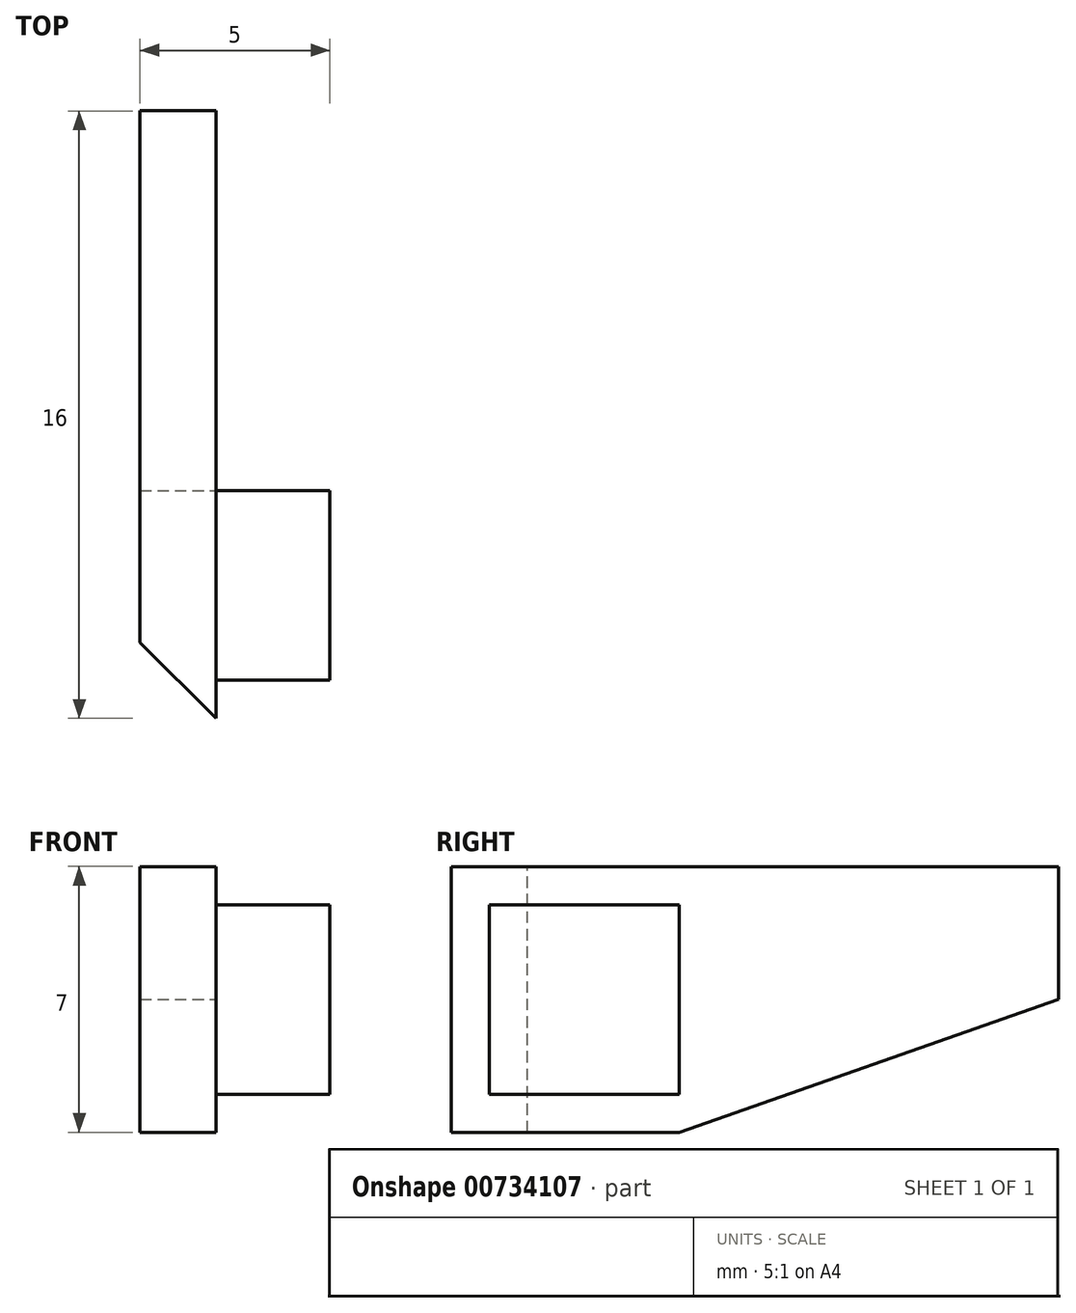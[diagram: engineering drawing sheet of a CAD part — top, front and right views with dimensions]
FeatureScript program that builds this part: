
annotation { "Feature Type Name" : "Feature", "Feature Type Description" : "" }
export const myFeature = defineFeature(function(context is Context, id is Id, definition is map)
    precondition{}
    {
        {
            var Q0;
            Q0=qCreatedBy(makeId("Right.planeOp"),FACE);
            var sketch = newSketch(context, id + "F0", { "sketchPlane" : qUnion([Q0])});
            skLineSegment(sketch, "E0.bottom", {"start": v(43.1, 34.6) * mm, "end": v(38.1, 34.6) * mm});
            skLineSegment(sketch, "E0.top", {"start": v(43.1, 29.6) * mm, "end": v(38.1, 29.6) * mm});
            skLineSegment(sketch, "E0.left", {"start": v(43.1, 34.6) * mm, "end": v(43.1, 29.6) * mm});
            skLineSegment(sketch, "E0.right", {"start": v(38.1, 34.6) * mm, "end": v(38.1, 29.6) * mm});
            skSolve(sketch);
        }
        {
            var Q0;
            Q0=makeQuery(id+"F0.imprint","IMPRINT",FACE,{"disambiguationData":[TD([[makeQuery(id+"F0.imprint","IMPRINT",EDGE,{"derivedFrom":sQuery(id+"F0.wireOp",EDGE,"E0.bottom")}),1.0]])]});
            extrude(context, id + "F1", {"entities" : qUnion([Q0]), "depth" : 3 * mm, "offsetDistance" : 25 * mm});
        }
        {
            var Q0;
            Q0=makeQuery(id+"F1.opExtrude","CAP_FACE",FACE,{"disambiguationData":[OSD([sQuery(id+"F0.wireOp",EDGE,"E0.bottom"),sQuery(id+"F0.wireOp",EDGE,"E0.top"),sQuery(id+"F0.wireOp",EDGE,"E0.left"),sQuery(id+"F0.wireOp",EDGE,"E0.right")])],"isStart":true});
            var sketch = newSketch(context, id + "F2", { "sketchPlane" : qUnion([Q0])});
            skLineSegment(sketch, "E1.bottom", {"start": v(-37.1, 35.6) * mm, "end": v(-53.1, 35.6) * mm});
            skLineSegment(sketch, "E1.top", {"start": v(-37.1, 28.6) * mm, "end": v(-53.1, 28.6) * mm});
            skLineSegment(sketch, "E1.left", {"start": v(-37.1, 35.6) * mm, "end": v(-37.1, 28.6) * mm});
            skLineSegment(sketch, "E1.right", {"start": v(-53.1, 35.6) * mm, "end": v(-53.1, 28.6) * mm});
            skLineSegment(sketch, "E2", {"start": v(-53.1, 32.1) * mm, "end": v(-43.1, 35.6) * mm});
            skLineSegment(sketch, "E3", {"start": v(-43.1, 35.6) * mm, "end": v(-43.1, 28.6) * mm});
            skLineSegment(sketch, "E4", {"start": v(-43.1, 28.6) * mm, "end": v(-53.1, 32.1) * mm});
            skLineSegment(sketch, "E5", {"start": v(-51.1, 35.6) * mm, "end": v(-51.1, 28.6) * mm});
            skSolve(sketch);
        }
        {
            var Q0;
            Q0=makeQuery(id+"F2.imprint","IMPRINT",FACE,{"disambiguationData":[TD([[makeQuery(id+"F2.imprint","IMPRINT",EDGE,{"derivedFrom":makeQuery(id+"F1.opExtrude","CAP_EDGE",EDGE,{"disambiguationData":[OSD([sQuery(id+"F0.wireOp",EDGE,"E0.bottom")])],"isStart":true})}),-1.0]])]});
            var Q1;
            {var subQ4=sQuery(id+"F2.wireOp",EDGE,"E1.left");Q1=makeQuery(id+"F2.imprint","IMPRINT",FACE,{"disambiguationData":[TD([[makeQuery(id+"F2.imprint","IMPRINT",EDGE,{"derivedFrom":subQ4}),-1.0]])]});}
            var Q2;
            {var subQ0=sQuery(id+"F2.wireOp",EDGE,"E3");var subQ4=makeQuery(id+"F2.imprint","INTERSECT",VERTEX,{"derivedFrom":[makeQuery(id+"F1.opExtrude","CAP_EDGE",EDGE,{"disambiguationData":[OSD([sQuery(id+"F0.wireOp",EDGE,"E0.bottom")])],"isStart":true}),subQ0]});Q2=makeQuery(id+"F2.imprint","IMPRINT",FACE,{"disambiguationData":[TD([[makeQuery(id+"F2.imprint","IMPRINT",EDGE,{"disambiguationData":[TD([[subQ4,-1.0]])],"derivedFrom":subQ0}),-1.0]])]});}
            var Q3;
            {var subQ1=sQuery(id+"F2.wireOp",EDGE,"E1.bottom");var subQ3=sQuery(id+"F2.wireOp",EDGE,"E5");var subQ4=makeQuery(id+"F2.imprint","INTERSECT",VERTEX,{"derivedFrom":[subQ1,subQ3]});Q3=makeQuery(id+"F2.imprint","IMPRINT",FACE,{"disambiguationData":[TD([[makeQuery(id+"F2.imprint","IMPRINT",EDGE,{"disambiguationData":[TD([[subQ4,-1.0]])],"derivedFrom":subQ3}),1.0]])]});}
            var Q4;
            {var subQ0=sQuery(id+"F2.wireOp",EDGE,"E1.right");var subQ1=sQuery(id+"F2.wireOp",EDGE,"E1.bottom");var subQ2=makeQuery(id+"F2.imprint","INTERSECT",VERTEX,{"derivedFrom":[subQ1,subQ0]});Q4=makeQuery(id+"F2.imprint","IMPRINT",FACE,{"disambiguationData":[TD([[makeQuery(id+"F2.imprint","IMPRINT",EDGE,{"disambiguationData":[TD([[subQ2,1.0]])],"derivedFrom":subQ1}),1.0]])]});}
            var Q5;
            {var subQ1=sQuery(id+"F2.wireOp",EDGE,"E2");var subQ3=sQuery(id+"F2.wireOp",EDGE,"E5");var subQ4=makeQuery(id+"F2.imprint","INTERSECT",VERTEX,{"derivedFrom":[subQ1,subQ3]});Q5=makeQuery(id+"F2.imprint","IMPRINT",FACE,{"disambiguationData":[TD([[makeQuery(id+"F2.imprint","IMPRINT",EDGE,{"disambiguationData":[TD([[subQ4,-1.0]])],"derivedFrom":subQ3}),-1.0]])]});}
            extrude(context, id + "F3", {"entities" : qUnion([Q0, Q1, Q2, Q3, Q4, Q5]), "operationType" : NewBodyOperationType.ADD, "depth" : 2 * mm, "offsetDistance" : 25 * mm});
        }
        {
            var Q0;
            Q0=makeQuery(id+"F3.opExtrude","CAP_EDGE",EDGE,{"disambiguationData":[OSD([sQuery(id+"F2.wireOp",EDGE,"E1.left")])],"isStart":false});
            chamfer(context, id + "F4", {"entities" : qUnion([Q0]), "width" : 2 * mm, "tangentPropagation" : true});
        }
    });
